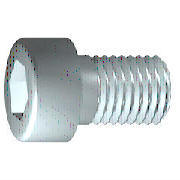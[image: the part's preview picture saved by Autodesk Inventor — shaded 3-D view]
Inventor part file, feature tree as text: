
AUTODESK INVENTOR PART (.ipt)
format: ipt  version: 2023.3 (Build 273359000, 359)  size: 187,904 bytes
history: native  units: mm (DEFAULTED — no unit token found)
features: sketch x2, other x1, extrude x1, plane x1, fillet x1
ambient origin geometry x7: Origin, YZ Plane, XY Plane, X Axis, Y Axis, Z Axis, Center Point
bodies: Solid1 (feature_tree)
feature tree (6):
  other  "Körper"
  extrude  "Loch"  Depth=2.0mm
  plane  "Work Plane1"
  fillet  "Fillet2"  Radius=2.0mm
  sketch  "Skizze1"  dims[d1=11.0mm d2=0.24548mm d3=2.0mm]
  sketch  "Skizze2"  dims[d4=1.0mm d5=60.0deg d6=2.0mm d7=2.0mm d8=1.732051mm d9=3.8mm d10=90.0deg d11=10.0mm d12=0.0mm d13=11.0mm d14=0.0mm d15=0.24538mm d16=0.24538mm d17=0.2mm d19=0.0mm d26=12.0mm d27=45.0deg d28=0.0mm d29=0.0mm d30=0.1mm]
